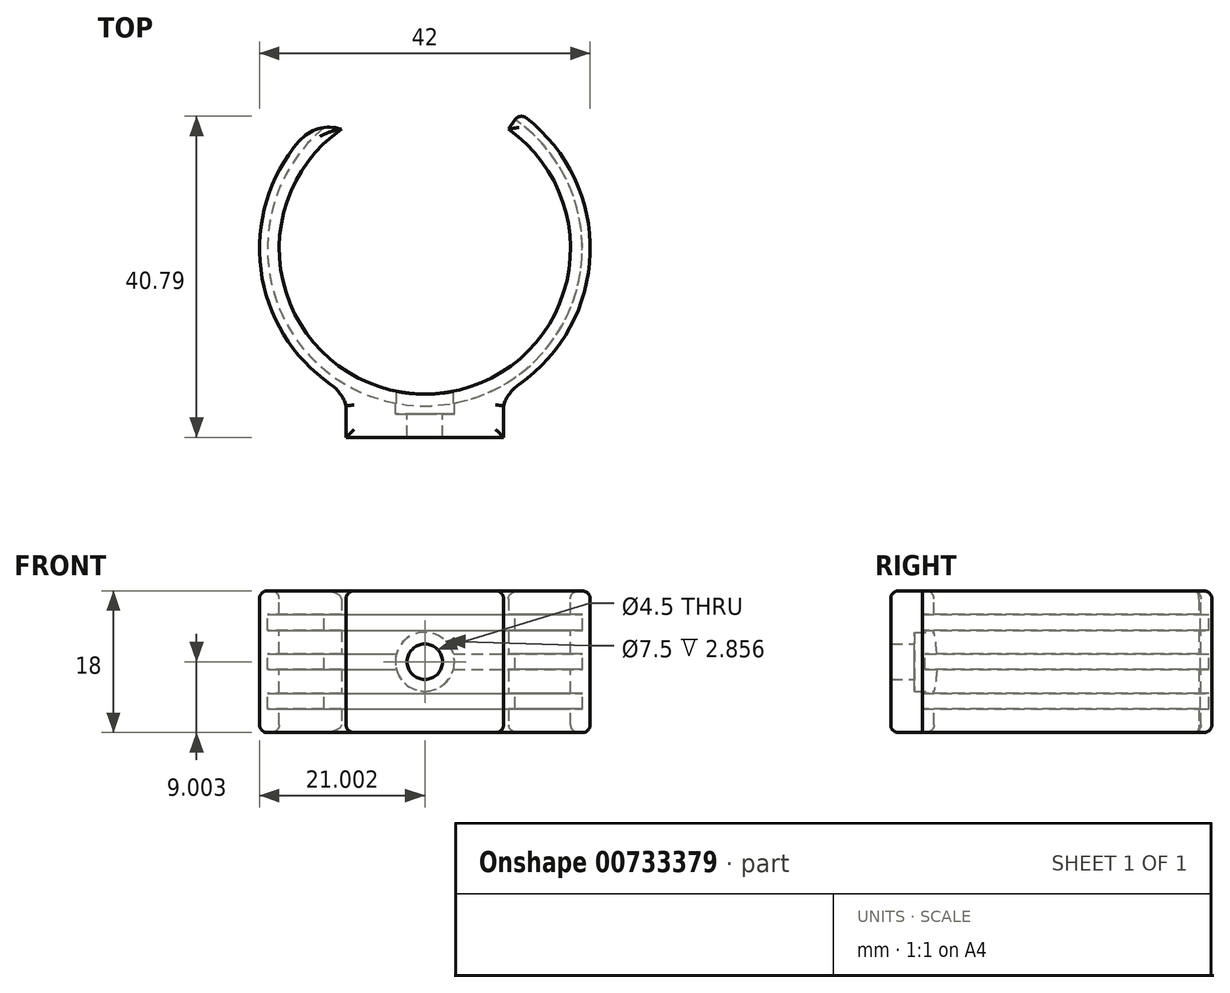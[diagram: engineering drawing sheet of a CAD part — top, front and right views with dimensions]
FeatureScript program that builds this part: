
annotation { "Feature Type Name" : "Feature", "Feature Type Description" : "" }
export const myFeature = defineFeature(function(context is Context, id is Id, definition is map)
    precondition{}
    {
        {
            var Q0;
            Q0=qCreatedBy(makeId("Front.planeOp"),FACE);
            var sketch = newSketch(context, id + "F0", { "sketchPlane" : qUnion([Q0])});
            skLineSegment(sketch, "E0", {"start": v(-48.7, 35.4) * mm, "end": v(-48.7, 17.4) * mm});
            skLineSegment(sketch, "E1", {"start": v(-46.2, 22.4) * mm, "end": v(-46.2, 25.4) * mm});
            skLineSegment(sketch, "E2", {"start": v(-46.2, 25.4) * mm, "end": v(-47.7, 25.4) * mm});
            skLineSegment(sketch, "E3", {"start": v(-47.7, 25.4) * mm, "end": v(-47.7, 27.4) * mm});
            skLineSegment(sketch, "E4", {"start": v(-47.7, 27.4) * mm, "end": v(-46.2, 27.4) * mm});
            skLineSegment(sketch, "E5", {"start": v(-46.2, 27.4) * mm, "end": v(-46.2, 30.4) * mm});
            skLineSegment(sketch, "E6", {"start": v(-46.2, 30.4) * mm, "end": v(-47.7, 30.4) * mm});
            skLineSegment(sketch, "E7", {"start": v(-47.7, 30.4) * mm, "end": v(-47.7, 32.4) * mm});
            skLineSegment(sketch, "E8", {"start": v(-47.7, 32.4) * mm, "end": v(-46.2, 32.4) * mm});
            skLineSegment(sketch, "E9", {"start": v(-46.2, 32.4) * mm, "end": v(-46.2, 35.4) * mm});
            skLineSegment(sketch, "E10", {"start": v(-46.2, 35.4) * mm, "end": v(-48.7, 35.4) * mm});
            skLineSegment(sketch, "E11", {"start": v(-27.7, 55.62) * mm, "end": v(-27.7, 6.27) * mm, "construction": true});
            skLineSegment(sketch, "E12", {"start": v(-46.2, 22.4) * mm, "end": v(-47.7, 22.4) * mm});
            skLineSegment(sketch, "E13", {"start": v(-47.7, 22.4) * mm, "end": v(-47.7, 20.4) * mm});
            skLineSegment(sketch, "E14", {"start": v(-47.7, 20.4) * mm, "end": v(-46.2, 20.4) * mm});
            skLineSegment(sketch, "E15", {"start": v(-46.2, 20.4) * mm, "end": v(-46.2, 17.4) * mm});
            skLineSegment(sketch, "E16", {"start": v(-46.2, 17.4) * mm, "end": v(-48.7, 17.4) * mm});
            skSolve(sketch);
        }
        {
            var Q0;
            Q0=makeQuery(id+"F0.imprint","IMPRINT",FACE,{"disambiguationData":[TD([[makeQuery(id+"F0.imprint","IMPRINT",EDGE,{"derivedFrom":sQuery(id+"F0.wireOp",EDGE,"E0")}),1.0]])]});
            var Q1;
            Q1=sQuery(id+"F0.wireOp",EDGE,"E11");
            revolve(context, id + "F1", {"surfaceOperationType" : NewSurfaceOperationType.NEW, "entities" : qUnion([Q0]), "axis" : qUnion([Q1]), "revolveType" : RevolveType.FULL});
        }
        {
            var Q0;
            Q0=qCreatedBy(makeId("Front.planeOp"),FACE);
            var sketch = newSketch(context, id + "F2", { "sketchPlane" : qUnion([Q0])});
            skLineSegment(sketch, "E17.0", {"start": v(-48.7, 35.4) * mm, "end": v(-6.7, 35.4) * mm});
            skLineSegment(sketch, "E18.0", {"start": v(-48.7, 17.4) * mm, "end": v(-6.7, 17.4) * mm});
            skLineSegment(sketch, "E19", {"start": v(-37.7, 17.4) * mm, "end": v(-37.7, 35.4) * mm});
            skLineSegment(sketch, "E20", {"start": v(-17.7, 35.4) * mm, "end": v(-17.7, 17.4) * mm});
            skLineSegment(sketch, "E21", {"start": v(-27.7, 42.35) * mm, "end": v(-27.7, 4.37) * mm, "construction": true});
            skPoint(sketch, "E21.startSnap0", {"position": v(-27.7, 35.4) * mm});
            skCircle(sketch, "E22", {"center": v(-27.7, 26.4) * mm, "radius": 2.25 * mm});
            skPoint(sketch, "E22.centerSnap0", {"position": v(-37.7, 26.4) * mm});
            skCircle(sketch, "E23", {"center": v(-27.7, 26.4) * mm, "radius": 3.75 * mm});
            skSolve(sketch);
        }
        {
            var Q0;
            Q0 = qSketchRegion(id + "F2", true);
            var Q1;
            Q1=makeQuery(id+"F2.imprint","IMPRINT",FACE,{"disambiguationData":[TD([[makeQuery(id+"F2.imprint","IMPRINT",EDGE,{"derivedFrom":sQuery(id+"F2.wireOp",EDGE,"E22")}),-1.0]])]});
            extrude(context, id + "F3", {"entities" : qUnion([Q0, Q1]), "operationType" : NewBodyOperationType.ADD, "depth" : 24 * mm, "offsetDistance" : 25 * mm, "hasSecondDirection" : true, "secondDirectionOppositeDirection" : false, "secondDirectionDepth" : 20 * mm});
        }
        {
            var Q0;
            Q0=makeQuery(id+"F3.boolean.opBoolean","INTERSECT",EDGE,{"disambiguationData":[OD(0.0)],"derivedFrom":[makeQuery(id+"F1.opRevolve","SWEPT_FACE",FACE,{"disambiguationData":[OSD([sQuery(id+"F0.wireOp",EDGE,"E0")])]}),makeQuery(id+"F3.opExtrude","CAP_FACE",FACE,{"disambiguationData":[OSD([sQuery(id+"F2.wireOp",EDGE,"E17.0"),sQuery(id+"F2.wireOp",EDGE,"E18.0"),sQuery(id+"F2.wireOp",EDGE,"E19"),sQuery(id+"F2.wireOp",EDGE,"E20")])],"isStart":true})]});
            var Q1;
            Q1=makeQuery(id+"F3.boolean.opBoolean","INTERSECT",EDGE,{"disambiguationData":[OD(1.0)],"derivedFrom":[makeQuery(id+"F1.opRevolve","SWEPT_FACE",FACE,{"disambiguationData":[OSD([sQuery(id+"F0.wireOp",EDGE,"E0")])]}),makeQuery(id+"F3.opExtrude","CAP_FACE",FACE,{"disambiguationData":[OSD([sQuery(id+"F2.wireOp",EDGE,"E17.0"),sQuery(id+"F2.wireOp",EDGE,"E18.0"),sQuery(id+"F2.wireOp",EDGE,"E19"),sQuery(id+"F2.wireOp",EDGE,"E20")])],"isStart":true})]});
            fillet(context, id + "F4", {"entities" : qUnion([Q0, Q1]), "radius" : 5 * mm, "tangentPropagation" : true, "allowEdgeOverflow" : false});
        }
        {
            var Q0;
            Q0=makeQuery(id+"F2.imprint","IMPRINT",FACE,{"disambiguationData":[TD([[makeQuery(id+"F2.imprint","IMPRINT",EDGE,{"derivedFrom":sQuery(id+"F2.wireOp",EDGE,"E22")}),1.0]])]});
            extrude(context, id + "F5", {"entities" : qUnion([Q0]), "operationType" : NewBodyOperationType.REMOVE, "endBound" : BoundingType.THROUGH_ALL, "depth" : 25 * mm, "offsetDistance" : 25 * mm});
        }
        {
            var Q0;
            Q0=makeQuery(id+"F2.imprint","IMPRINT",FACE,{"disambiguationData":[TD([[makeQuery(id+"F2.imprint","IMPRINT",EDGE,{"derivedFrom":sQuery(id+"F2.wireOp",EDGE,"E22")}),-1.0]])]});
            extrude(context, id + "F6", {"entities" : qUnion([Q0]), "operationType" : NewBodyOperationType.REMOVE, "depth" : 21 * mm, "offsetDistance" : 25 * mm});
        }
        {
            var Q0;
            Q0=makeQuery(id+"F3.boolean.opBoolean","MERGE",FACE,{"derivedFrom":[makeQuery(id+"F1.opRevolve","SWEPT_FACE",FACE,{"disambiguationData":[OSD([sQuery(id+"F0.wireOp",EDGE,"E16")])]}),makeQuery(id+"F3.opExtrude","SWEPT_FACE",FACE,{"disambiguationData":[OSD([sQuery(id+"F2.wireOp",EDGE,"E18.0")])]})]});
            var sketch = newSketch(context, id + "F7", { "sketchPlane" : qUnion([Q0])});
            skLineSegment(sketch, "E24", {"start": v(-27.7, 34) * mm, "end": v(-27.7, -35.95) * mm, "construction": true});
            skPoint(sketch, "E24.startSnap0", {"position": v(-27.7, 24) * mm});
            skLineSegment(sketch, "E25", {"start": v(-27.7, 0) * mm, "end": v(-11.51, -23.13) * mm});
            skLineSegment(sketch, "E26", {"start": v(-11.51, -23.13) * mm, "end": v(-43.9, -23.13) * mm});
            skLineSegment(sketch, "E27", {"start": v(-43.9, -23.13) * mm, "end": v(-27.7, 0) * mm});
            skSolve(sketch);
        }
        {
            var Q0;
            {var subQ0=sQuery(id+"F7.wireOp",EDGE,"E25");var subQ1=sQuery(id+"F0.wireOp",EDGE,"E16");var subQ2=makeQuery(id+"F1.opRevolve","SWEPT_EDGE",EDGE,{"disambiguationData":[OSD([sQuery(id+"F0.wireOp",EDGE,"E0"),subQ1])]});var subQ3=makeQuery(id+"F7.imprint","INTERSECT",VERTEX,{"derivedFrom":[subQ2,subQ0]});Q0=makeQuery(id+"F7.imprint","IMPRINT",FACE,{"disambiguationData":[TD([[makeQuery(id+"F7.imprint","IMPRINT",EDGE,{"disambiguationData":[TD([[subQ3,1.0]])],"derivedFrom":subQ0}),-1.0]])]});}
            extrude(context, id + "F8", {"entities" : qUnion([Q0]), "operationType" : NewBodyOperationType.REMOVE, "endBound" : BoundingType.THROUGH_ALL, "oppositeDirection" : true, "depth" : 25 * mm, "offsetDistance" : 25 * mm});
        }
        {
            var Q0;
            Q0=makeQuery(id+"F8.boolean.opBoolean","COPY",EDGE,{"derivedFrom":makeQuery(id+"F8.opExtrude","SWEPT_EDGE",EDGE,{"disambiguationData":[OSD([sQuery(id+"F0.wireOp",EDGE,"E0"),sQuery(id+"F0.wireOp",EDGE,"E16"),sQuery(id+"F7.wireOp",EDGE,"E27")])]})});
            var Q1;
            Q1=makeQuery(id+"F8.boolean.opBoolean","COPY",EDGE,{"derivedFrom":makeQuery(id+"F8.opExtrude","SWEPT_EDGE",EDGE,{"disambiguationData":[OSD([sQuery(id+"F0.wireOp",EDGE,"E0"),sQuery(id+"F0.wireOp",EDGE,"E16"),sQuery(id+"F7.wireOp",EDGE,"E25")])]})});
            fillet(context, id + "F9", {"entities" : qUnion([Q0, Q1]), "radius" : 5 * mm, "tangentPropagation" : true, "allowEdgeOverflow" : false});
        }
        {
            var Q0;
            {var subQ5=sQuery(id+"F0.wireOp",EDGE,"E0");var subQ7=sQuery(id+"F0.wireOp",EDGE,"E10");Q0=makeQuery(id+"F8.boolean.opBoolean","SPLIT",EDGE,{"disambiguationData":[TD([makeQuery(id+"F8.opExtrude","SWEPT_FACE",FACE,{"disambiguationData":[OSD([sQuery(id+"F7.wireOp",EDGE,"E27")])]})])],"derivedFrom":makeQuery(id+"F1.opRevolve","SWEPT_EDGE",EDGE,{"disambiguationData":[OSD([subQ5,subQ7])]})});}
            var Q1;
            {var subQ5=makeQuery(id+"F1.opRevolve","SWEPT_FACE",FACE,{"disambiguationData":[OSD([sQuery(id+"F0.wireOp",EDGE,"E10")])]});var subQ10=sQuery(id+"F0.wireOp",EDGE,"E0");var subQ11=makeQuery(id+"F1.opRevolve","SWEPT_FACE",FACE,{"disambiguationData":[OSD([subQ10])]});Q1=makeQuery(id+"F8.boolean.opBoolean","SPLIT",FACE,{"disambiguationData":[TD([makeQuery(id+"F8.opExtrude","SWEPT_FACE",FACE,{"disambiguationData":[OSD([sQuery(id+"F7.wireOp",EDGE,"E25")])]})])],"derivedFrom":makeQuery(id+"F3.boolean.opBoolean","SPLIT",FACE,{"disambiguationData":[TD([subQ5])],"derivedFrom":subQ11})});}
            var Q2;
            {var subQ5=makeQuery(id+"F1.opRevolve","SWEPT_FACE",FACE,{"disambiguationData":[OSD([sQuery(id+"F0.wireOp",EDGE,"E10")])]});var subQ10=sQuery(id+"F0.wireOp",EDGE,"E0");var subQ11=makeQuery(id+"F1.opRevolve","SWEPT_FACE",FACE,{"disambiguationData":[OSD([subQ10])]});Q2=makeQuery(id+"F8.boolean.opBoolean","SPLIT",FACE,{"disambiguationData":[TD([makeQuery(id+"F8.opExtrude","SWEPT_FACE",FACE,{"disambiguationData":[OSD([sQuery(id+"F7.wireOp",EDGE,"E27")])]})])],"derivedFrom":makeQuery(id+"F3.boolean.opBoolean","SPLIT",FACE,{"disambiguationData":[TD([subQ5])],"derivedFrom":subQ11})});}
            var Q3;
            Q3=makeQuery(id+"F3.boolean.opBoolean","MERGE",FACE,{"derivedFrom":[makeQuery(id+"F1.opRevolve","SWEPT_FACE",FACE,{"disambiguationData":[OSD([sQuery(id+"F0.wireOp",EDGE,"E16")])]}),makeQuery(id+"F3.opExtrude","SWEPT_FACE",FACE,{"disambiguationData":[OSD([sQuery(id+"F2.wireOp",EDGE,"E18.0")])]})]});
            var Q4;
            Q4=makeQuery(id+"F3.boolean.opBoolean","MERGE",FACE,{"derivedFrom":[makeQuery(id+"F1.opRevolve","SWEPT_FACE",FACE,{"disambiguationData":[OSD([sQuery(id+"F0.wireOp",EDGE,"E10")])]}),makeQuery(id+"F3.opExtrude","SWEPT_FACE",FACE,{"disambiguationData":[OSD([sQuery(id+"F2.wireOp",EDGE,"E17.0")])]})]});
            fillet(context, id + "F10", {"entities" : qUnion([Q0, Q1, Q2, Q3, Q4]), "radius" : 1 * mm, "tangentPropagation" : true, "allowEdgeOverflow" : false});
        }
    });
